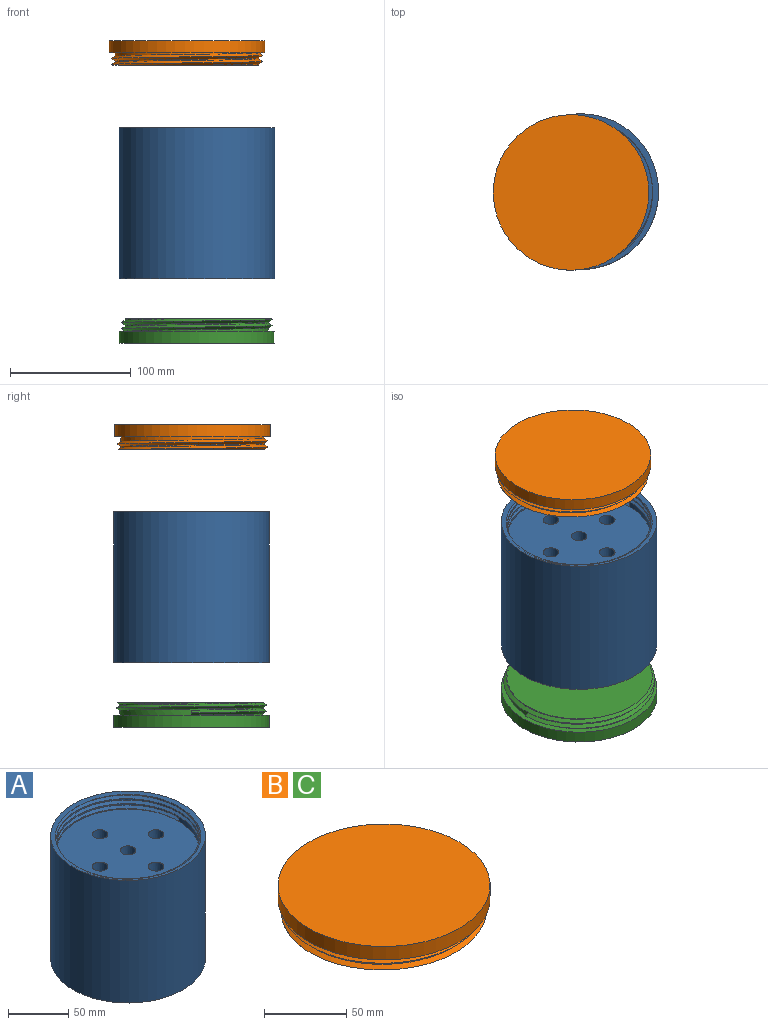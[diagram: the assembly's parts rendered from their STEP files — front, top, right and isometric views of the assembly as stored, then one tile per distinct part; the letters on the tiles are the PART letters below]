
ASSEMBLY  parts=3 mates=1
PART A: 19 faces, bbox 131.5x147.1x131.4 mm
  f0: plane 119x119mm, normal (0,0,1), area 10458.4mm2, adj f3,f4,f5,f6,f7,f8
  f1: cylinder r=64.5mm len=129mm, axis (0,0,1), area 50658.2mm2, adj f2,f9
  f2: plane 130.58x130.58mm, normal (0,0,-1), area 1365.5mm2, adj f1,f12,f13,f14
  f3: cone r=6.5mm half-angle=1.8deg, axis (0,0,1), area 3086mm2, adj f0,f10
  f4: cone r=6.5mm half-angle=1.8deg, axis (0,0,1), area 3086mm2, adj f0,f10
  f5: cone r=6.5mm half-angle=1.8deg, axis (0,0,1), area 3086mm2, adj f0,f10
  f6: cone r=3mm half-angle=1.8deg, axis (0,0,1), area 3086mm2, adj f0,f10
  f7: cone r=6.5mm half-angle=1.8deg, axis (0,0,1), area 3086mm2, adj f0,f10
  f8: cylinder r=59.5mm len=119mm, axis (0,0,-1), area 2020.6mm2, adj f0,f9,f16,f17,f18
  f9: plane 131.46x131.46mm, normal (0,0,1), area 1511.3mm2, adj f1,f8,f17,f18
  f10: plane 119x119mm, normal (0,0,-1), area 10949.1mm2, adj f3,f4,f5,f6,f7,f11
  f11: cylinder r=59.5mm len=119mm, axis (0,0,-1), area 1412.5mm2, adj f10,f12,f13,f14,f15
  f12: cone r=60.5mm half-angle=45deg, axis (0,0,-1), area 207.6mm2, adj f2,f11,f13,f14
  f13: bspline ~144.68x125.3mm, area 2492.5mm2, adj f2,f11,f12,f14,f15
  f14: bspline ~144.68x125.3mm, area 1989.2mm2, adj f2,f11,f12,f13,f15
  f15: plane 3.64x3.15mm, normal (0,-1,0), area 5.7mm2, adj f11,f13,f14
  f16: plane 3.64x3.15mm, normal (0,1,0), area 5.7mm2, adj f8,f17,f18
  f17: bspline ~144.68x125.3mm, area 3427.6mm2, adj f8,f9,f16,f18
  f18: bspline ~144.68x125.3mm, area 3930.2mm2, adj f8,f9,f16,f17
PART B: 8 faces, bbox 131.4x146.8x24.7 mm
  f0: bspline ~144.43x125.08mm, area 2507.6mm2, adj f1,f2,f6,f7
  f1: bspline ~144.43x125.08mm, area 1957.3mm2, adj f0,f2,f6,f7
  f2: cylinder r=59.5mm len=119mm, axis (0,0,1), area 1351.6mm2, adj f0,f1,f5,f6,f7
  f3: cylinder r=64.5mm len=129mm, axis (0,0,-1), area 4052.7mm2, adj f4,f5
  f4: plane 129x129mm, normal (0,0,1), area 13069.8mm2, adj f3
  f5: plane 129x129mm, normal (0,0,-1), area 1947.8mm2, adj f2,f3
  f6: plane 123.73x123.73mm, normal (0,0,-1), area 11582.7mm2, adj f0,f1,f2
  f7: plane 3.99x3.04mm, normal (0,1,0), area 6.1mm2, adj f0,f1,f2
PART C: same geometry as B
PLACE A t=(2.19,0,-101.14)mm fixed
PLACE B t=(-5.86,-0.9,-24.05)mm
PLACE C rot(axis=(0,1,0),180deg) t=(2.19,0,-254.64)mm
MATE cylindrical A.f5 <-> C.f2  axis (0,0,-1) through (2.19,0,-201.14)mm
